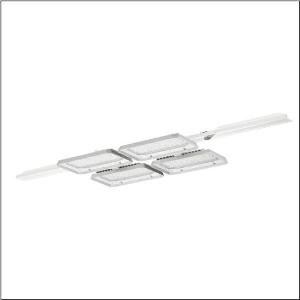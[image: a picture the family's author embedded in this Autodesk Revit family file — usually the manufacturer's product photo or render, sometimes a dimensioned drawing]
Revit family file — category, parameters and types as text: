
# Revit family: highbay_11_51hla1d24nla
name_source: partatom
category: Lighting Fixtures
units: mm (PartAtom-declared; Revit-internal decimal feet)

## family parameters
Cut with Voids When Loaded = No
Host = Face
Light Source = No
Part Type = Normal
Room Calculation Point = No
Round Connector Dimension = Use Diameter
Shared = No

## types (1)
- --- (1 x LED, 32370 lm, 189.7 W, 4000K)
    Apparent Load = 759 VA
    CIE Flux Codes = 88 95 99 100 99
    Color Rendering = 80
    Color Temperature = 4000K
    Default Elevation = 1800 mm
    Description = Highbay 11, LED high bay luminaire, end cap, primary light control with lens, of PMMA, light emission: direct distribution, primary light characteristic: symmetric, installation type: recessed, for 2x 2x LED, rated luminous flux: 32.370lm, luminous efficacy: 171lm/W, light colour: 840, colour temperature: 4000K, control gear: ECG DALI, with system connector, mains connection: 230..240V, AC, 50/60Hz, rated input power: 190W, LED unit, of diecast aluminium, unplated, bead blasted, silver, for tool-free mounting of luminaire to Licross® trunking rail, length: 1.500mm, width: 500mm, height: 65mm, housing, of diecast aluminium, uncoated, bead blasted, silver, fixing on rail side, of aluminium, anodised, metallic grey, end cap, of PC, grey, protection rating (complete): IP64, insulation class (complete): insulation class I (protective earthing), certification: CE, UKCA, protection symbol: D, impact resistance: IK08 with glass or PC cover, permissible operating ambient temperature: -35..+45°C, corresponds to IFS (International Featured Standards) requirements for safety and quality in the food industry, packaging unit: 1 piece
    Height = 105 mm
    Lamp = 1 x LED
    Lamp Light Flux = 32370 lm
    Lamp Power = 189.7 W
    Lamp count = 1
    Length = 1500 mm
    Luminous efficacy = 171 lm/W
    Manufacturer = Siteco
    ModVariant = No
    Model = 51HLA1D24NLA
    Mounting Place = Ceiling
    Mounting Type = Pendant
    Number of Poles = 1
    OnlyDefault = Yes
    Power Factor = 1
    Product Name = Highbay 11
    Product group = LED high bay luminaire
    ProductGroupID = 903
    Protection Class = Protection class I
    Protection Degree = IP 64
    RLX_Detail_Level = 1
    RLX_Emergency_Light_Flux = 0 lm
    RLX_Emergency_Type = 0
    RLX_Emergency_Type_DB = No
    RlxData = <blob elided: 88353 chars, md5=378548de>
    Socket = socket
    Standby Power = 0 W
    System Light Flux = 129480 lm
    System Power = 759 W
    Type Comments = factory setting: luminous flux: 100 % | dim-lin: 254 | 535 mA
    Type Image = l_1004707.jpg
    URL = http://relux.com
    VarID = @adj_143189
    Voltage = 0 V
    Weight = 0.00 kg
    Width = 500 mm

## geometry (parser evidence)
native form markers: Blend x4, Sweep x20
no freeform markers — native parametric forms only
